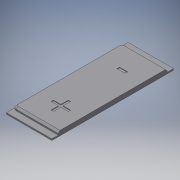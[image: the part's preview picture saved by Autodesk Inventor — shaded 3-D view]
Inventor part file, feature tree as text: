
AUTODESK INVENTOR PART (.ipt)
format: ipt  version: 2016 SP2 (Build 200236200, 236)  size: 161,792 bytes
history: native  units: mm
features: sketch x4, other x3
ambient origin geometry x8: Origin, YZ Plane, XZ Plane, XY Plane, X Axis, Y Axis, Z Axis, Center Point
bodies: Volumenkörper1 (feature_tree)
feature tree (7):
  other  "Button.ipt"
  other  "Volumenkörper1::Button.ipt"
  other  "Bezeichnung1"
  sketch  "Skizze1"  dims[d0=10.0mm]
  sketch  "Skizze2"
  sketch  "Skizze3"
  sketch  "Skizze4"
